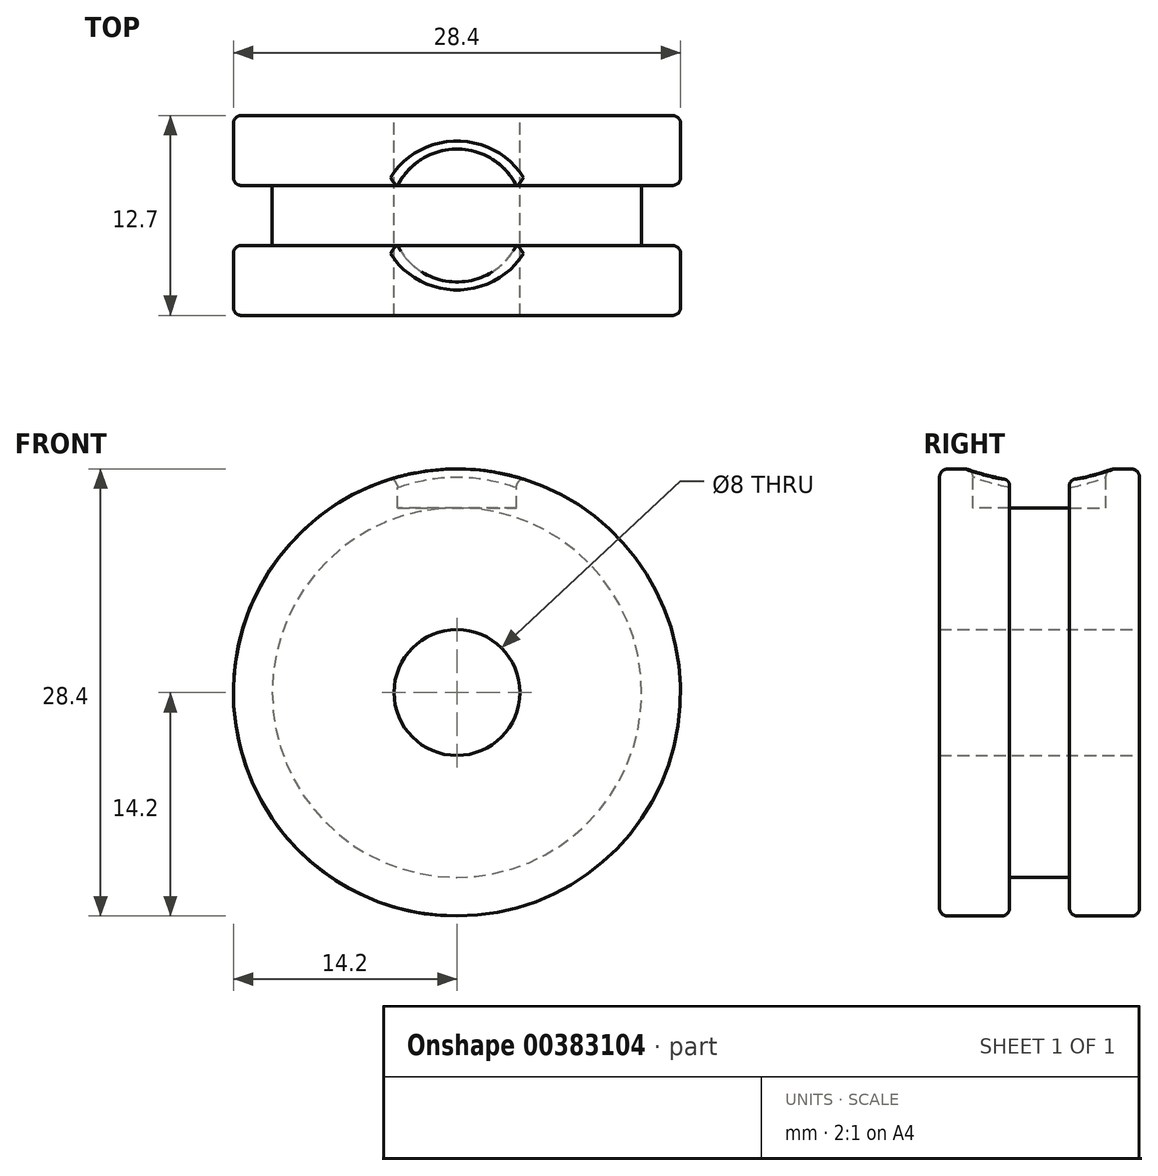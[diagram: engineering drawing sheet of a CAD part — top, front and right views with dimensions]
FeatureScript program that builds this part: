
annotation { "Feature Type Name" : "Feature", "Feature Type Description" : "" }
export const myFeature = defineFeature(function(context is Context, id is Id, definition is map)
    precondition{}
    {
        {
            var Q0;
            Q0=qCreatedBy(makeId("Front.planeOp"),FACE);
            var sketch = newSketch(context, id + "F0", { "sketchPlane" : qUnion([Q0])});
            skCircle(sketch, "E0.cCircle", {"center": v(0, 0) * mm, "radius": 12.21 * mm, "construction": true});
            skLineSegment(sketch, "E0.0", {"start": v(-3.97, 12.21) * mm, "end": v(3.97, 12.21) * mm, "construction": true});
            skLineSegment(sketch, "E0.1", {"start": v(3.97, 12.21) * mm, "end": v(10.4, 7.55) * mm, "construction": true});
            skLineSegment(sketch, "E0.2", {"start": v(10.4, 7.55) * mm, "end": v(12.84, 0) * mm, "construction": true});
            skLineSegment(sketch, "E0.3", {"start": v(12.84, 0) * mm, "end": v(10.4, -7.55) * mm, "construction": true});
            skLineSegment(sketch, "E0.4", {"start": v(10.4, -7.55) * mm, "end": v(3.97, -12.21) * mm, "construction": true});
            skLineSegment(sketch, "E0.5", {"start": v(3.97, -12.21) * mm, "end": v(-3.97, -12.21) * mm, "construction": true});
            skLineSegment(sketch, "E0.6", {"start": v(-3.97, -12.21) * mm, "end": v(-10.4, -7.55) * mm, "construction": true});
            skLineSegment(sketch, "E0.7", {"start": v(-10.4, -7.55) * mm, "end": v(-12.84, 0) * mm, "construction": true});
            skLineSegment(sketch, "E0.8", {"start": v(-12.84, 0) * mm, "end": v(-10.4, 7.55) * mm, "construction": true});
            skLineSegment(sketch, "E0.9", {"start": v(-10.4, 7.55) * mm, "end": v(-3.97, 12.21) * mm, "construction": true});
            skPoint(sketch, "E0.0.midPoint", {"position": v(0, 12.21) * mm});
            skCircle(sketch, "E1.cCircle", {"center": v(0, 0) * mm, "radius": 14.2 * mm});
            skLineSegment(sketch, "E1.0", {"start": v(-4.61, 14.2) * mm, "end": v(4.61, 14.2) * mm, "construction": true});
            skLineSegment(sketch, "E1.1", {"start": v(4.61, 14.2) * mm, "end": v(12.08, 8.78) * mm, "construction": true});
            skLineSegment(sketch, "E1.2", {"start": v(12.08, 8.78) * mm, "end": v(14.93, 0) * mm, "construction": true});
            skLineSegment(sketch, "E1.3", {"start": v(14.93, 0) * mm, "end": v(12.08, -8.78) * mm, "construction": true});
            skLineSegment(sketch, "E1.4", {"start": v(12.08, -8.78) * mm, "end": v(4.61, -14.2) * mm, "construction": true});
            skLineSegment(sketch, "E1.5", {"start": v(4.61, -14.2) * mm, "end": v(-4.61, -14.2) * mm, "construction": true});
            skLineSegment(sketch, "E1.6", {"start": v(-4.61, -14.2) * mm, "end": v(-12.08, -8.78) * mm, "construction": true});
            skLineSegment(sketch, "E1.7", {"start": v(-12.08, -8.78) * mm, "end": v(-14.93, 0) * mm, "construction": true});
            skLineSegment(sketch, "E1.8", {"start": v(-14.93, 0) * mm, "end": v(-12.08, 8.78) * mm, "construction": true});
            skLineSegment(sketch, "E1.9", {"start": v(-12.08, 8.78) * mm, "end": v(-4.61, 14.2) * mm, "construction": true});
            skPoint(sketch, "E1.0.midPoint", {"position": v(0, 14.2) * mm});
            skCircle(sketch, "E2", {"center": v(0, 0) * mm, "radius": 4 * mm});
            skSolve(sketch);
        }
        {
            var Q0;
            Q0 = qSketchRegion(id + "F0", true);
            extrude(context, id + "F1", {"entities" : qUnion([Q0]), "endBound" : BoundingType.SYMMETRIC, "depth" : 12.7 * mm});
        }
        {
            var Q0;
            Q0=qCreatedBy(makeId("Top.planeOp"),FACE);
            cPlane(context, id + "F2", {"entities" : qUnion([Q0]), "cplaneType" : CPlaneType.OFFSET, "offset" : 14.22 * mm, "width" : 152.4 * mm, "height" : 152.4 * mm});
        }
        {
            var Q0;
            Q0=qCreatedBy(id+"F2.planeOp",FACE);
            var sketch = newSketch(context, id + "F3", { "sketchPlane" : qUnion([Q0])});
            skCircle(sketch, "E3", {"center": v(0, 0) * mm, "radius": 4.22 * mm});
            skSolve(sketch);
        }
        {
            var Q0;
            Q0 = qSketchRegion(id + "F3", true);
            extrude(context, id + "F4", {"entities" : qUnion([Q0]), "operationType" : NewBodyOperationType.REMOVE, "oppositeDirection" : true, "depth" : 2.5 * mm});
        }
        {
            var Q0;
            Q0=qCreatedBy(makeId("Right.planeOp"),FACE);
            var sketch = newSketch(context, id + "F5", { "sketchPlane" : qUnion([Q0])});
            skLineSegment(sketch, "E4.bottom", {"start": v(-1.9, 21.03) * mm, "end": v(1.9, 21.03) * mm});
            skLineSegment(sketch, "E4.top", {"start": v(-1.9, 11.73) * mm, "end": v(1.9, 11.73) * mm});
            skLineSegment(sketch, "E4.left", {"start": v(-1.9, 21.03) * mm, "end": v(-1.9, 11.73) * mm});
            skLineSegment(sketch, "E4.right", {"start": v(1.9, 21.03) * mm, "end": v(1.9, 11.73) * mm});
            skPoint(sketch, "E4.middle", {"position": v(0, 16.38) * mm});
            skSolve(sketch);
        }
        {
            var Q0;
            Q0 = qSketchRegion(id + "F5", true);
            var Q1;
            Q1=makeQuery(id+"F1.opExtrude","CAP_EDGE",EDGE,{"disambiguationData":[OSD([sQuery(id+"F0.wireOp",EDGE,"E1.cCircle")])],"isStart":false});
            revolve(context, id + "F6", {"operationType" : NewBodyOperationType.REMOVE, "entities" : qUnion([Q0]), "axis" : qUnion([Q1]), "revolveType" : RevolveType.FULL, "oppositeDirection" : true});
        }
        {
            var Q0;
            {var subQ1=sQuery(id+"F0.wireOp",EDGE,"E1.cCircle");Q0=makeQuery(id+"F6.boolean.opBoolean","SPLIT",FACE,{"disambiguationData":[TD([makeQuery(id+"F6.opRevolve","SWEPT_FACE",FACE,{"disambiguationData":[OSD([sQuery(id+"F5.wireOp",EDGE,"E4.right")])]})])],"derivedFrom":makeQuery(id+"F1.opExtrude","SWEPT_FACE",FACE,{"disambiguationData":[OSD([subQ1])]})});}
            var Q1;
            {var subQ1=sQuery(id+"F0.wireOp",EDGE,"E1.cCircle");Q1=makeQuery(id+"F6.boolean.opBoolean","SPLIT",FACE,{"disambiguationData":[TD([makeQuery(id+"F6.opRevolve","SWEPT_FACE",FACE,{"disambiguationData":[OSD([sQuery(id+"F5.wireOp",EDGE,"E4.left")])]})])],"derivedFrom":makeQuery(id+"F1.opExtrude","SWEPT_FACE",FACE,{"disambiguationData":[OSD([subQ1])]})});}
            fillet(context, id + "F7", {"entities" : qUnion([Q0, Q1]), "radius" : 0.5 * mm, "tangentPropagation" : true, "allowEdgeOverflow" : false});
        }
    });
